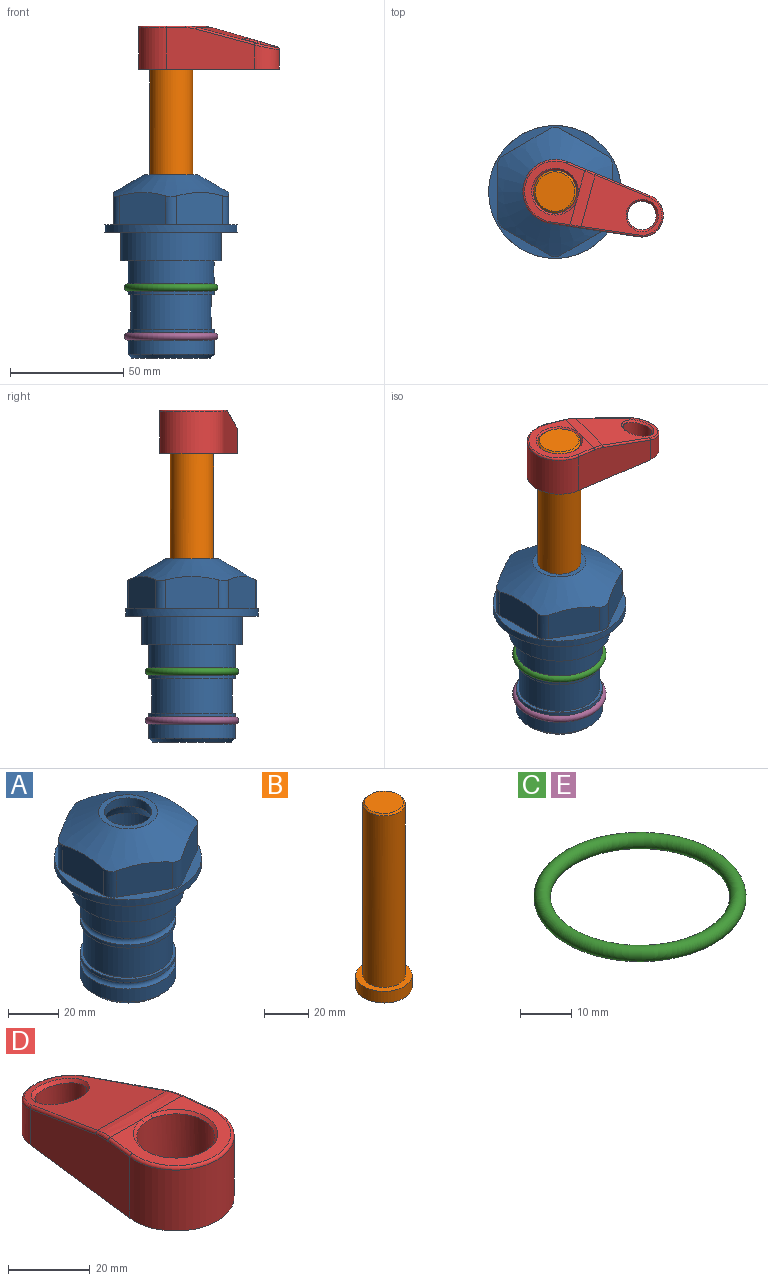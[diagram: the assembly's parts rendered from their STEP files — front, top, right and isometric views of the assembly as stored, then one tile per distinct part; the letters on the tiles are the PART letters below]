
ASSEMBLY  parts=5 mates=3
PART A: 36 faces, bbox 58.7x58.7x81 mm
  f0: cylinder r=17.78mm len=35.56mm, axis (0,0,1), area 1670.8mm2, adj f23,f24,f31
  f1: cylinder r=19.05mm len=38.1mm, axis (0,0,1), area 1191.9mm2, adj f26,f27,f30
  f2: plane 58.66x58.66mm, normal (0,0,-1), area 1150.6mm2, adj f3,f28
  f3: cylinder r=29.33mm len=58.66mm, axis (0,0,-1), area 585.1mm2, adj f2,f4
  f4: plane 58.66x58.66mm, normal (0,0,1), area 475.9mm2, adj f3,f5,f6,f7,f8,f9,f10,f11
  f5: plane 20.32x14.34mm, normal (-0.5,0.87,0), area 324.4mm2, adj f4,f15,f16,f17
  f6: plane 20.32x14.34mm, normal (0.5,0.87,0), area 324.4mm2, adj f4,f14,f15,f17
  f7: plane 23.48x14.34mm, normal (1,0,0), area 324.4mm2, adj f4,f13,f14,f17
  f8: plane 20.32x14.34mm, normal (0.5,-0.87,0), area 324.4mm2, adj f4,f12,f13,f17
  f9: plane 20.32x14.34mm, normal (-0.5,-0.87,0), area 324.4mm2, adj f4,f11,f12,f17
  f10: plane 23.48x14.34mm, normal (-1,0,0), area 324.4mm2, adj f4,f11,f16,f17
  f11: cylinder r=5.08mm len=12.85mm, axis (0,0,-1), area 67.2mm2, adj f4,f9,f10,f17
  f12: cylinder r=5.08mm len=12.85mm, axis (0,0,-1), area 67.2mm2, adj f4,f8,f9,f17
  f13: cylinder r=5.08mm len=12.85mm, axis (0,0,-1), area 67.2mm2, adj f4,f7,f8,f17
  f14: cylinder r=5.08mm len=12.85mm, axis (0,0,-1), area 67.2mm2, adj f4,f6,f7,f17
  f15: cylinder r=5.08mm len=12.85mm, axis (0,0,-1), area 67.2mm2, adj f4,f5,f6,f17
  f16: cylinder r=5.08mm len=12.85mm, axis (0,0,-1), area 67.2mm2, adj f4,f5,f10,f17
  f17: cone r=11.73mm half-angle=60deg, axis (0,0,-1), area 2071.8mm2, adj f5,f6,f7,f8,f9,f10,f11,f12
  f18: plane 23.46x23.46mm, normal (0,0,1), area 147.4mm2, adj f17,f35
  f19: plane 34.93x34.93mm, normal (0,0,-1), area 958mm2, adj f29
  f20: cylinder r=19.05mm len=38.1mm, axis (0,0,1), area 760.1mm2, adj f21,f29
  f21: torus R=19.05mm, axis (0,0,1), area 565.3mm2, adj f20,f22
  f22: cylinder r=19.05mm len=38.1mm, axis (0,0,1), area 190mm2, adj f21,f23
  f23: plane 38.1x38.1mm, normal (0,0,1), area 146.9mm2, adj f0,f22
  f24: plane 38.1x38.1mm, normal (0,0,-1), area 146.9mm2, adj f0,f25
  f25: cylinder r=19.05mm len=38.1mm, axis (0,0,1), area 190mm2, adj f24,f26
  f26: torus R=19.05mm, axis (0,0,1), area 565.3mm2, adj f1,f25
  f27: plane 44.45x44.45mm, normal (0,0,-1), area 411.7mm2, adj f1,f28
  f28: cylinder r=22.23mm len=44.45mm, axis (0,0,1), area 1773.5mm2, adj f2,f27
  f29: cone r=19.05mm half-angle=45deg, axis (0,0,1), area 257.5mm2, adj f19,f20
  f30: cylinder r=3.17mm len=6.75mm, axis (-1,0,0), area 128mm2, adj f1,f33
  f31: cylinder r=3.17mm len=6.35mm, axis (-1,0,0), area 102.5mm2, adj f0,f33
  f32: plane 25.4x25.4mm, normal (0,0,1), area 506.7mm2, adj f33
  f33: cylinder r=12.7mm len=66.42mm, axis (0,0,-1), area 5236.2mm2, adj f30,f31,f32,f34
  f34: cone r=9.53mm half-angle=30deg, axis (0,0,-1), area 443.4mm2, adj f33,f35
  f35: cylinder r=9.53mm len=19.05mm, axis (0,0,-1), area 240.9mm2, adj f18,f34
PART B: 6 faces, bbox 25.4x25.4x101.6 mm
  f0: plane 17.46x17.46mm, normal (0,0,1), area 239.5mm2, adj f5
  f1: plane 25.4x25.4mm, normal (0,0,-1), area 506.7mm2, adj f2
  f2: cylinder r=12.7mm len=25.4mm, axis (0,0,1), area 506.7mm2, adj f1,f3
  f3: plane 25.4x25.4mm, normal (0,0,1), area 221.7mm2, adj f2,f4
  f4: cylinder r=9.53mm len=94.46mm, axis (0,0,1), area 5653mm2, adj f3,f5
  f5: cone r=8.73mm half-angle=45deg, axis (0,0,-1), area 64.4mm2, adj f0,f4
PART C: 1 faces, bbox 44.7x44.7x3.2 mm
  f0: torus R=19.05mm, axis (0,0,1), area 1193.9mm2
PART D: 31 faces, bbox 31.7x65.5x19.8 mm
  f0: plane 39.12x18.26mm, normal (0.99,0.12,0), area 612.2mm2, adj f1,f4,f7,f11,f13,f15
  f1: cylinder r=9.53mm len=18.91mm, axis (0,0,-1), area 296.1mm2, adj f0,f2,f7,f17
  f2: plane 39.12x18.26mm, normal (-0.99,0.12,0), area 612.2mm2, adj f1,f4,f7,f12,f14,f16
  f3: cylinder r=6.35mm len=12.7mm, axis (0,0,-1), area 362.4mm2, adj f7,f18
  f4: cylinder r=14.29mm len=28.58mm, axis (0,0,-1), area 882.2mm2, adj f0,f2,f7,f10
  f5: cylinder r=9.53mm len=19.05mm, axis (0,0,-1), area 1092.6mm2, adj f7,f19,f20
  f6: plane 26.99x23.69mm, normal (0,0,1), area 216.2mm2, adj f9,f10,f11,f12,f19
  f7: plane 63.5x28.58mm, normal (0,0,-1), area 661.8mm2, adj f0,f1,f2,f3,f4,f5,f22,f23
  f8: plane 33.52x23.6mm, normal (0,0.26,0.97), area 486mm2, adj f9,f15,f16,f17,f18
  f9: cylinder r=19.05mm len=24.72mm, axis (1,0,0), area 120.4mm2, adj f6,f8,f13,f14,f20
  f10: torus R=13.49mm, axis (0,0,1), area 59mm2, adj f4,f6,f11,f12
  f11: cylinder r=0.79mm len=8.67mm, axis (0.12,-0.99,0), area 10.8mm2, adj f0,f6,f10,f13
  f12: cylinder r=0.79mm len=8.67mm, axis (0.12,0.99,0), area 10.8mm2, adj f2,f6,f10,f14
  f13: bspline ~4.95x1.42mm, area 6.1mm2, adj f0,f9,f11,f15
  f14: bspline ~4.95x1.42mm, area 6.1mm2, adj f2,f9,f12,f16
  f15: cylinder r=0.79mm len=25.95mm, axis (0.12,-0.96,0.26), area 32.9mm2, adj f0,f8,f13,f17
  f16: cylinder r=0.79mm len=25.95mm, axis (0.12,0.96,-0.26), area 32.9mm2, adj f2,f8,f14,f17
  f17: bspline ~18.91x8.38mm, area 30mm2, adj f1,f8,f15,f16
  f18: bspline ~14.29x14.29mm, area 48.3mm2, adj f3,f8
  f19: cone r=9.53mm half-angle=45deg, axis (0,0,1), area 66.5mm2, adj f5,f6,f20
  f20: bspline ~3.22x0.96mm, area 3.5mm2, adj f5,f9,f19
  f21: plane 2.75x2.72mm, normal (0,0,-1), area 2.9mm2, adj f23,f25,f28
  f22: plane 23.05x15.88mm, normal (-0.99,-0.12,0), area 323.6mm2, adj f7,f25,f26,f27,f28,f29
  f23: plane 23.05x15.88mm, normal (0.99,-0.12,0), area 323.6mm2, adj f7,f21,f25,f27,f28,f30
  f24: cylinder r=9.53mm len=10.69mm, axis (0,0,-1), area 114.7mm2, adj f7,f27,f29,f30
  f25: cylinder r=12.7mm len=20.59mm, axis (0,0,-1), area 381.1mm2, adj f7,f21,f22,f23,f26,f28
  f26: plane 2.75x2.72mm, normal (0,0,-1), area 2.9mm2, adj f22,f25,f28
  f27: plane 19.72x18.37mm, normal (0,-0.26,-0.97), area 291.8mm2, adj f22,f23,f24,f28,f29,f30
  f28: cylinder r=15.88mm len=19.92mm, axis (1,0,0), area 54.8mm2, adj f21,f22,f23,f25,f26,f27
  f29: cylinder r=1.59mm len=11mm, axis (0,0,-1), area 34.7mm2, adj f7,f22,f24,f27
  f30: cylinder r=1.59mm len=11mm, axis (0,0,-1), area 34.7mm2, adj f7,f23,f24,f27
PART E: same geometry as C
PLACE A at identity fixed
PLACE B rot(axis=(0,0,-1),105.3deg) t=(0,0,27.55)mm
PLACE C at identity
PLACE D rot(axis=(0,0,-1),105.3deg) t=(0,0,27.55)mm
PLACE E t=(0,0,-21.59)mm
MATE fastened C.f0 <-> A.f0  axis (0,0,1) through (0,0,-24.51)mm
MATE cylindrical B.f2 <-> A.f0  axis (0,0,-1) through (0,0,-10.55)mm
MATE fastened B.f2 <-> D.f4  axis (0,0,1) through (0,0,91.05)mm
